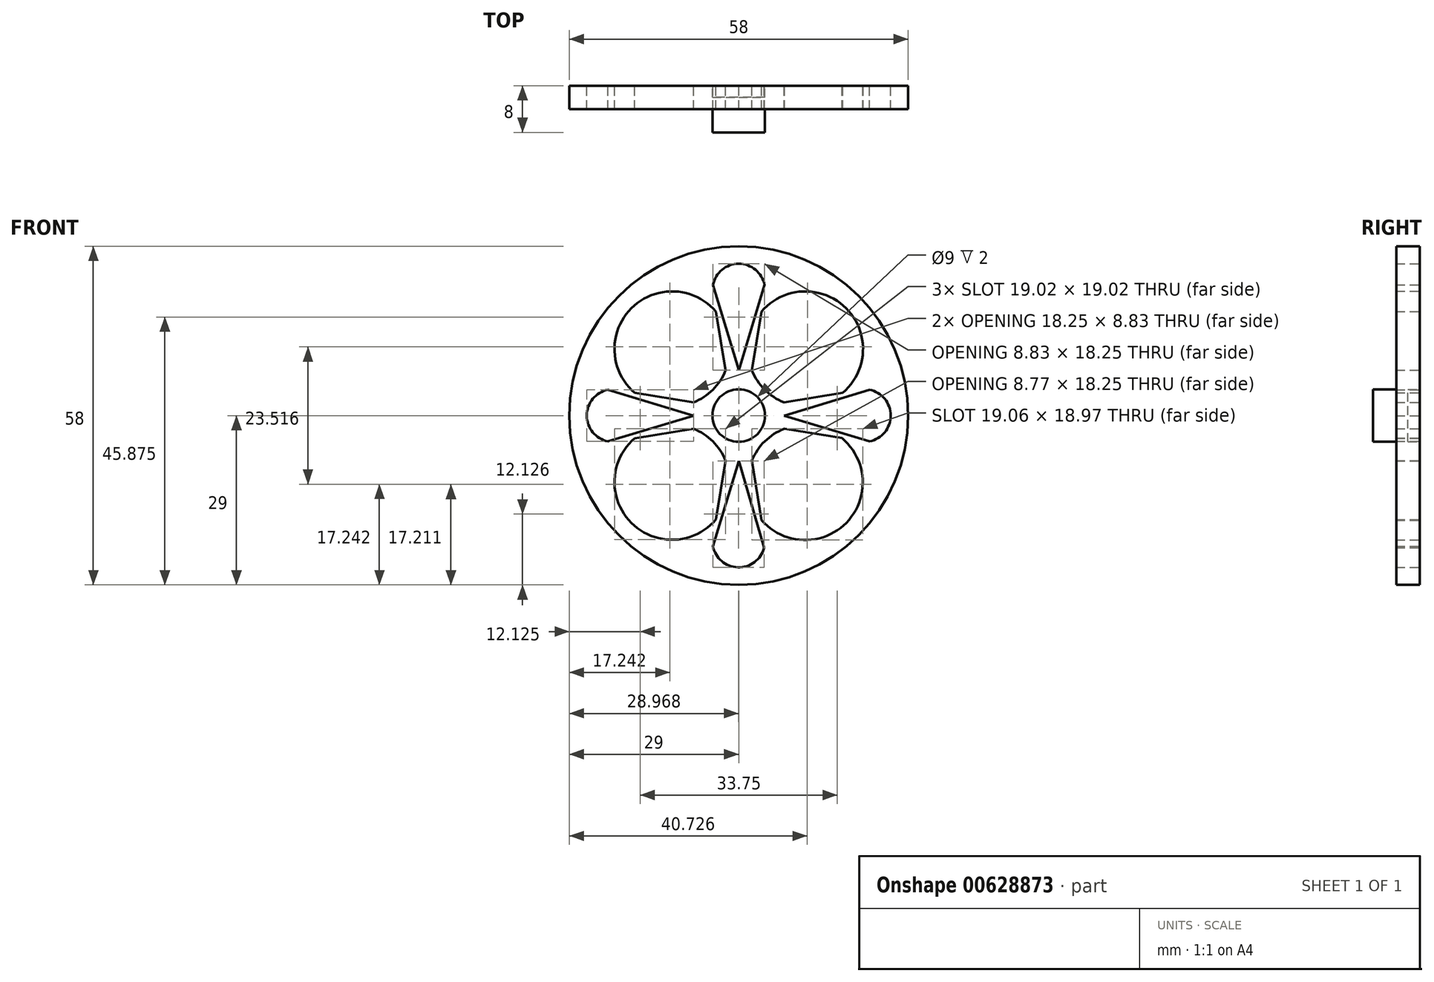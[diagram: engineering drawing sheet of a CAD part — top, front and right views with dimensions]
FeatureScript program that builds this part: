
annotation { "Feature Type Name" : "Feature", "Feature Type Description" : "" }
export const myFeature = defineFeature(function(context is Context, id is Id, definition is map)
    precondition{}
    {
        {
            var Q0;
            Q0=qCreatedBy(makeId("Front.planeOp"),FACE);
            var sketch = newSketch(context, id + "F0", { "sketchPlane" : qUnion([Q0])});
            skCircle(sketch, "E0", {"center": v(0, 0) * mm, "radius": 27 * mm});
            skCircle(sketch, "E1", {"center": v(0, 0) * mm, "radius": 4.5 * mm});
            skCircle(sketch, "E2", {"center": v(0, 0) * mm, "radius": 29 * mm});
            skArc(sketch, "E3", {"start": v(-22.37, 4.42) * mm, "mid": v(-26, 0) * mm, "end": v(-22.37, -4.42) * mm});
            skArc(sketch, "E4", {"start": v(4.42, 22.37) * mm, "mid": v(0, 26) * mm, "end": v(-4.42, 22.37) * mm});
            skArc(sketch, "E5", {"start": v(22.37, -4.42) * mm, "mid": v(26, 0) * mm, "end": v(22.37, 4.42) * mm});
            skArc(sketch, "E6", {"start": v(-4.42, -22.37) * mm, "mid": v(-0.14, -26) * mm, "end": v(4.35, -22.65) * mm});
            skPoint(sketch, "E7.orphan", {"position": v(-55.65, 0) * mm});
            skLineSegment(sketch, "E8", {"start": v(-17.8, 3.9) * mm, "end": v(-7.75, 2.25) * mm});
            skLineSegment(sketch, "E9", {"start": v(-17.8, -3.9) * mm, "end": v(-7.75, -2.25) * mm});
            skLineSegment(sketch, "E10", {"start": v(-2.25, -7.75) * mm, "end": v(-3.9, -17.8) * mm});
            skLineSegment(sketch, "E11", {"start": v(2.24, -7.7) * mm, "end": v(3.92, -17.93) * mm});
            skLineSegment(sketch, "E12", {"start": v(7.8, -2.26) * mm, "end": v(17.66, -3.87) * mm});
            skLineSegment(sketch, "E13", {"start": v(7.75, 2.25) * mm, "end": v(17.8, 3.9) * mm});
            skLineSegment(sketch, "E14", {"start": v(2.25, 7.75) * mm, "end": v(3.9, 17.8) * mm});
            skArc(sketch, "E15", {"start": v(7.8, -2.26) * mm, "mid": v(4.46, -4.4) * mm, "end": v(2.24, -7.7) * mm});
            skPoint(sketch, "E15.third.point", {"position": v(18.33, -18.44) * mm});
            skArc(sketch, "E16", {"start": v(17.8, 3.9) * mm, "mid": v(18.38, 18.38) * mm, "end": v(3.9, 17.8) * mm});
            skPoint(sketch, "E16.third.point", {"position": v(16.77, 19.7) * mm});
            skArc(sketch, "E17", {"start": v(-17.8, -3.9) * mm, "mid": v(-18.38, -18.38) * mm, "end": v(-3.9, -17.8) * mm});
            skPoint(sketch, "E17.third.point", {"position": v(-19.92, -16.4) * mm});
            skArc(sketch, "E18", {"start": v(-7.75, 2.25) * mm, "mid": v(-4.43, 4.43) * mm, "end": v(-2.25, 7.75) * mm});
            skPoint(sketch, "E18.third.point", {"position": v(-19.3, 17.32) * mm});
            skLineSegment(sketch, "E19", {"start": v(0, 7.75) * mm, "end": v(-4.42, 22.37) * mm});
            skLineSegment(sketch, "E20", {"start": v(4.42, 22.37) * mm, "end": v(0, 7.75) * mm});
            skLineSegment(sketch, "E21", {"start": v(7.75, 0) * mm, "end": v(14.26, 1.97) * mm});
            skLineSegment(sketch, "E22", {"start": v(22.37, -4.42) * mm, "end": v(7.75, 0) * mm});
            skLineSegment(sketch, "E23", {"start": v(-7.75, 0) * mm, "end": v(-22.37, 4.42) * mm});
            skLineSegment(sketch, "E24", {"start": v(-22.37, -4.42) * mm, "end": v(-7.75, 0) * mm});
            skLineSegment(sketch, "E25", {"start": v(0, -7.75) * mm, "end": v(-4.42, -22.37) * mm});
            skLineSegment(sketch, "E26", {"start": v(4.35, -22.65) * mm, "end": v(0, -7.75) * mm});
            skArc(sketch, "E27.trimOffspring", {"start": v(-2.25, -7.75) * mm, "mid": v(-4.43, -4.43) * mm, "end": v(-7.75, -2.25) * mm});
            skArc(sketch, "E28.trimOffspring", {"start": v(3.92, -17.93) * mm, "mid": v(18.41, -18.36) * mm, "end": v(17.66, -3.87) * mm});
            skLineSegment(sketch, "E29", {"start": v(14.26, 1.97) * mm, "end": v(22.37, 4.42) * mm});
            skArc(sketch, "E30.trimOffspring", {"start": v(2.25, 7.75) * mm, "mid": v(4.43, 4.43) * mm, "end": v(7.75, 2.25) * mm});
            skArc(sketch, "E31.trimOffspring", {"start": v(-3.9, 17.8) * mm, "mid": v(-18.38, 18.38) * mm, "end": v(-17.8, 3.9) * mm});
            skLineSegment(sketch, "E32.trimOffspring", {"start": v(-3.9, 17.8) * mm, "end": v(-2.25, 7.75) * mm});
            skSolve(sketch);
        }
        {
            var Q0;
            Q0=makeQuery(id+"F0.imprint","IMPRINT",FACE,{"disambiguationData":[TD([[makeQuery(id+"F0.imprint","IMPRINT",EDGE,{"derivedFrom":sQuery(id+"F0.wireOp",EDGE,"E1")}),1.0]])]});
            extrude(context, id + "F1", {"entities" : qUnion([Q0]), "depth" : 8 * mm, "offsetDistance" : 25 * mm});
        }
        {
            var Q0;
            Q0=makeQuery(id+"F0.imprint","IMPRINT",FACE,{"disambiguationData":[TD([[makeQuery(id+"F0.imprint","IMPRINT",EDGE,{"derivedFrom":sQuery(id+"F0.wireOp",EDGE,"E0")}),1.0]])]});
            var Q1;
            Q1=makeQuery(id+"F0.imprint","IMPRINT",FACE,{"disambiguationData":[TD([[makeQuery(id+"F0.imprint","IMPRINT",EDGE,{"derivedFrom":sQuery(id+"F0.wireOp",EDGE,"E0")}),-1.0]])]});
            extrude(context, id + "F2", {"entities" : qUnion([Q0, Q1]), "operationType" : NewBodyOperationType.ADD, "depth" : 4 * mm, "offsetDistance" : 25 * mm});
        }
        {
            var Q0;
            Q0=makeQuery(id+"F0.imprint","IMPRINT",FACE,{"disambiguationData":[TD([[makeQuery(id+"F0.imprint","IMPRINT",EDGE,{"derivedFrom":sQuery(id+"F0.wireOp",EDGE,"E1")}),1.0]])]});
            extrude(context, id + "F3", {"entities" : qUnion([Q0]), "operationType" : NewBodyOperationType.REMOVE, "depth" : 2 * mm, "offsetDistance" : 25 * mm});
        }
    });
